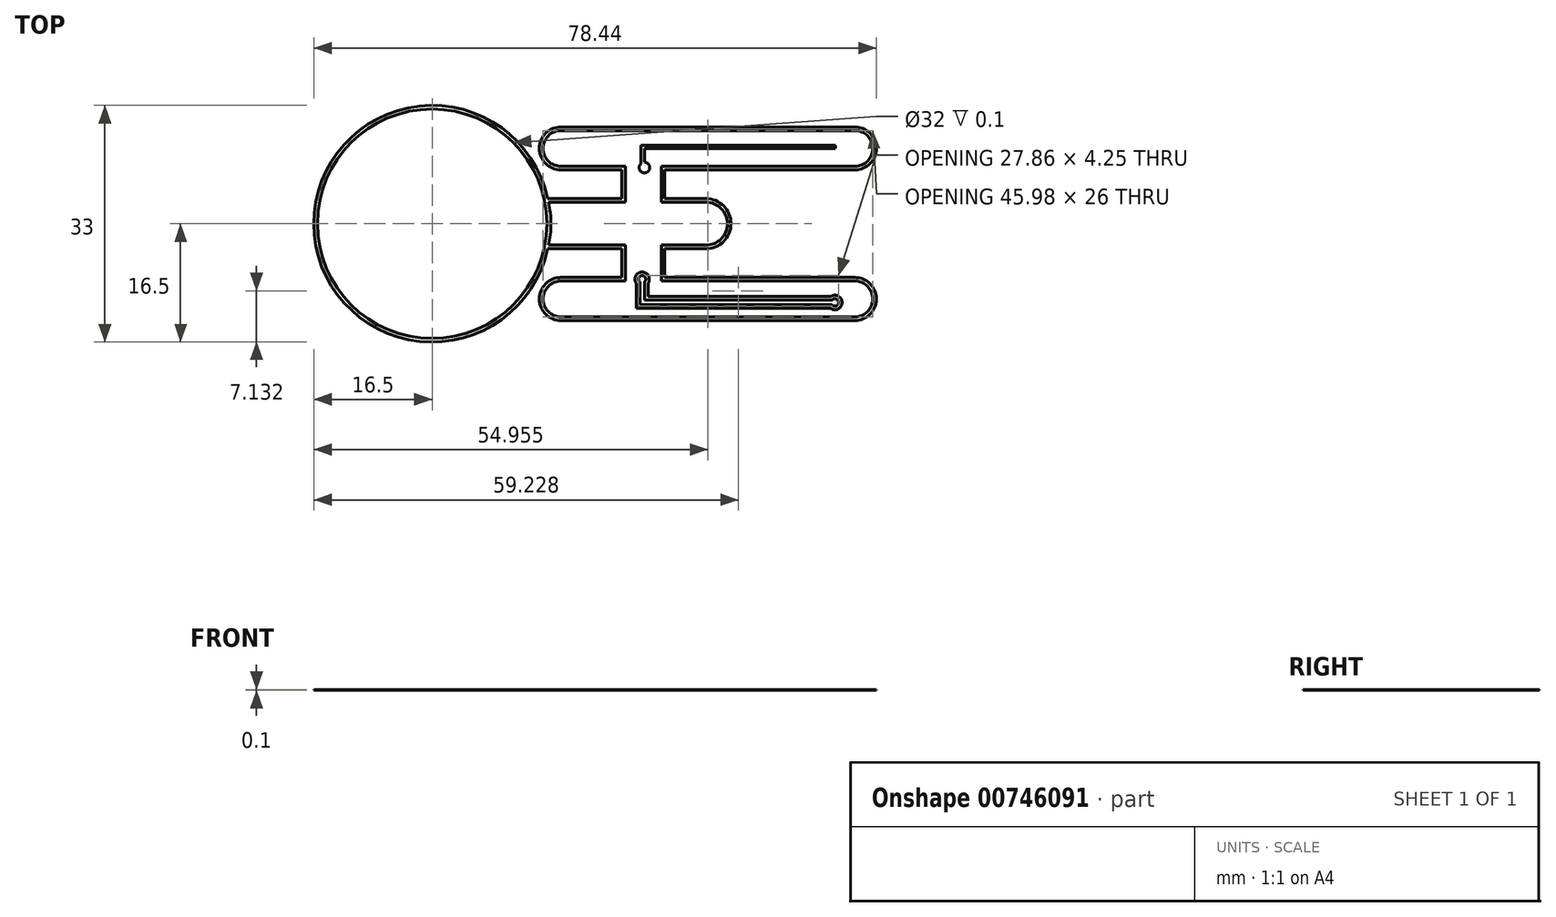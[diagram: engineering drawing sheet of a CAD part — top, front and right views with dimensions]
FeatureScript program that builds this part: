
annotation { "Feature Type Name" : "Feature", "Feature Type Description" : "" }
export const myFeature = defineFeature(function(context is Context, id is Id, definition is map)
    precondition{}
    {
        {
            var Q0;
            Q0=qCreatedBy(makeId("Top.planeOp"),FACE);
            var sketch = newSketch(context, id + "F0", { "sketchPlane" : qUnion([Q0])});
            skCircle(sketch, "E0", {"center": v(0, 0) * mm, "radius": 16 * mm});
            skLineSegment(sketch, "E1", {"start": v(16.22, 3) * mm, "end": v(26.94, 3) * mm});
            skLineSegment(sketch, "E2", {"start": v(38.16, -3) * mm, "end": v(31.94, -3) * mm});
            skLineSegment(sketch, "E3", {"start": v(31.94, 3) * mm, "end": v(31.94, 8) * mm});
            skLineSegment(sketch, "E4", {"start": v(31.94, -3) * mm, "end": v(31.94, -8) * mm});
            skLineSegment(sketch, "E5", {"start": v(26.94, 3) * mm, "end": v(26.94, 8) * mm});
            skPoint(sketch, "E5.startSnap0", {"position": v(26.94, -3) * mm});
            skLineSegment(sketch, "E6", {"start": v(26.94, -3) * mm, "end": v(26.94, -8) * mm});
            skLineSegment(sketch, "E7", {"start": v(17.97, 8) * mm, "end": v(26.94, 8) * mm});
            skLineSegment(sketch, "E8", {"start": v(58.94, 8) * mm, "end": v(58.94, 8) * mm});
            skLineSegment(sketch, "E9", {"start": v(58.94, 13) * mm, "end": v(17.97, 13) * mm});
            skLineSegment(sketch, "E10", {"start": v(17.97, -8) * mm, "end": v(26.94, -8) * mm});
            skLineSegment(sketch, "E11", {"start": v(58.94, -13) * mm, "end": v(17.97, -13) * mm});
            skArc(sketch, "E12", {"start": v(58.94, 8) * mm, "mid": v(61.44, 10.5) * mm, "end": v(58.94, 13) * mm});
            skArc(sketch, "E13", {"start": v(58.94, -13) * mm, "mid": v(61.44, -10.5) * mm, "end": v(58.94, -8) * mm});
            skArc(sketch, "E14", {"start": v(38.16, -3) * mm, "mid": v(41.16, 0) * mm, "end": v(38.16, 3) * mm});
            skLineSegment(sketch, "E15.trimOffspring", {"start": v(58.94, 13) * mm, "end": v(58.94, 13) * mm});
            skArc(sketch, "E16", {"start": v(17.97, 13) * mm, "mid": v(15.47, 10.5) * mm, "end": v(17.97, 8) * mm});
            skArc(sketch, "E17", {"start": v(17.97, -8) * mm, "mid": v(15.47, -10.5) * mm, "end": v(17.97, -13) * mm});
            skArc(sketch, "E18.0", {"start": v(58.94, 7.5) * mm, "mid": v(61.94, 10.5) * mm, "end": v(58.94, 13.5) * mm});
            skLineSegment(sketch, "E19.trimOffspring", {"start": v(31.94, 8) * mm, "end": v(58.94, 8) * mm});
            skLineSegment(sketch, "E20.trimOffspring", {"start": v(31.94, -8) * mm, "end": v(58.94, -8) * mm});
            skLineSegment(sketch, "E21.trimOffspring", {"start": v(31.94, 3) * mm, "end": v(38.16, 3) * mm});
            skLineSegment(sketch, "E22.trimOffspring", {"start": v(26.94, -3) * mm, "end": v(16.22, -3) * mm});
            skLineSegment(sketch, "E23.0", {"start": v(32.44, 7.5) * mm, "end": v(58.94, 7.5) * mm});
            skLineSegment(sketch, "E24.0", {"start": v(58.94, 13.5) * mm, "end": v(17.97, 13.5) * mm});
            skArc(sketch, "E25.0", {"start": v(17.97, 13.5) * mm, "mid": v(14.97, 10.5) * mm, "end": v(17.97, 7.5) * mm});
            skLineSegment(sketch, "E26.0", {"start": v(17.97, 7.5) * mm, "end": v(26.44, 7.5) * mm});
            skLineSegment(sketch, "E27.0", {"start": v(26.44, 3.5) * mm, "end": v(26.44, 7.5) * mm});
            skLineSegment(sketch, "E28.0", {"start": v(16.12, 3.5) * mm, "end": v(26.44, 3.5) * mm});
            skArc(sketch, "E29.0", {"start": v(16.22, 3) * mm, "mid": v(-16.5, 0) * mm, "end": v(16.22, -3) * mm});
            skLineSegment(sketch, "E30.0", {"start": v(26.44, -3.5) * mm, "end": v(16.12, -3.5) * mm});
            skLineSegment(sketch, "E31.0", {"start": v(26.44, -3.5) * mm, "end": v(26.44, -7.5) * mm});
            skLineSegment(sketch, "E32.0", {"start": v(17.97, -7.5) * mm, "end": v(26.44, -7.5) * mm});
            skArc(sketch, "E33.0", {"start": v(17.97, -7.5) * mm, "mid": v(14.97, -10.5) * mm, "end": v(17.97, -13.5) * mm});
            skLineSegment(sketch, "E34.0", {"start": v(58.94, -13.5) * mm, "end": v(17.97, -13.5) * mm});
            skArc(sketch, "E35.0", {"start": v(58.94, -13.5) * mm, "mid": v(61.94, -10.5) * mm, "end": v(58.94, -7.5) * mm});
            skLineSegment(sketch, "E36.0", {"start": v(32.44, -7.5) * mm, "end": v(58.94, -7.5) * mm});
            skLineSegment(sketch, "E37.0", {"start": v(32.44, -3.5) * mm, "end": v(32.44, -7.5) * mm});
            skLineSegment(sketch, "E38.0", {"start": v(38.16, -3.5) * mm, "end": v(32.44, -3.5) * mm});
            skArc(sketch, "E39.0", {"start": v(38.16, -3.5) * mm, "mid": v(41.66, 0) * mm, "end": v(38.16, 3.5) * mm});
            skLineSegment(sketch, "E40.0", {"start": v(32.44, 3.5) * mm, "end": v(38.16, 3.5) * mm});
            skLineSegment(sketch, "E41.0", {"start": v(32.44, 3.5) * mm, "end": v(32.44, 7.5) * mm});
            skPoint(sketch, "E42.orphan", {"position": v(15.72, -3) * mm});
            skArc(sketch, "E43", {"start": v(16.22, -3) * mm, "mid": v(16.56, 0) * mm, "end": v(16.22, 3) * mm});
            skSolve(sketch);
        }
        {
            var Q0;
            Q0=makeQuery(id+"F0.imprint","IMPRINT",FACE,{"disambiguationData":[TD([[makeQuery(id+"F0.imprint","IMPRINT",EDGE,{"derivedFrom":sQuery(id+"F0.wireOp",EDGE,"E0")}),-1.0]])]});
            var Q1;
            {var subQ1=sQuery(id+"F0.wireOp",EDGE,"E1");Q1=makeQuery(id+"F0.imprint","IMPRINT",FACE,{"disambiguationData":[TD([[makeQuery(id+"F0.imprint","IMPRINT",EDGE,{"derivedFrom":subQ1}),1.0]])]});}
            extrude(context, id + "F1", {"entities" : qUnion([Q0, Q1]), "depth" : .1 * mm, "offsetDistance" : 25 * mm});
        }
        {
            var Q0;
            Q0=qCreatedBy(makeId("Top.planeOp"),FACE);
            var sketch = newSketch(context, id + "F2", { "sketchPlane" : qUnion([Q0])});
            skLineSegment(sketch, "E44", {"start": v(56.23, 10.46) * mm, "end": v(29.6, 10.46) * mm});
            skLineSegment(sketch, "E45", {"start": v(29.6, 10.46) * mm, "end": v(29.6, 7.83) * mm});
            skLineSegment(sketch, "E46", {"start": v(55.74, -10.67) * mm, "end": v(29.6, -10.67) * mm});
            skLineSegment(sketch, "E47", {"start": v(29.6, -10.67) * mm, "end": v(29.6, -8.13) * mm});
            skLineSegment(sketch, "E48.0", {"start": v(29.1, 10.96) * mm, "end": v(29.1, 7.83) * mm});
            skLineSegment(sketch, "E48.1", {"start": v(56.23, 10.96) * mm, "end": v(29.1, 10.96) * mm});
            skLineSegment(sketch, "E49.0", {"start": v(28.96, -11.32) * mm, "end": v(28.96, -8.13) * mm});
            skLineSegment(sketch, "E49.1", {"start": v(55.74, -11.32) * mm, "end": v(28.96, -11.32) * mm});
            skLineSegment(sketch, "E50", {"start": v(29.6, 7.83) * mm, "end": v(29.1, 7.83) * mm});
            skLineSegment(sketch, "E51", {"start": v(56.23, 10.96) * mm, "end": v(56.23, 10.46) * mm});
            skCircle(sketch, "E52", {"center": v(29.6, 7.83) * mm, "radius": 0.74 * mm});
            skLineSegment(sketch, "E53.trimOffspring", {"start": v(29.04, -7.74) * mm, "end": v(28.96, -7.74) * mm});
            skArc(sketch, "E54", {"start": v(29.6, -8.13) * mm, "mid": v(29.28, -7.24) * mm, "end": v(28.96, -8.13) * mm});
            skArc(sketch, "E55", {"start": v(55.74, -11.32) * mm, "mid": v(56.66, -11) * mm, "end": v(55.74, -10.67) * mm});
            skArc(sketch, "E56.0", {"start": v(55.54, -11.82) * mm, "mid": v(57.16, -11) * mm, "end": v(55.54, -10.17) * mm});
            skLineSegment(sketch, "E56.1", {"start": v(30.1, -10.17) * mm, "end": v(30.1, -8.31) * mm});
            skArc(sketch, "E56.2", {"start": v(30.1, -8.31) * mm, "mid": v(29.28, -6.74) * mm, "end": v(28.46, -8.31) * mm});
            skLineSegment(sketch, "E56.3", {"start": v(55.54, -10.17) * mm, "end": v(30.1, -10.17) * mm});
            skLineSegment(sketch, "E56.4", {"start": v(28.46, -11.82) * mm, "end": v(28.46, -8.31) * mm});
            skLineSegment(sketch, "E56.5", {"start": v(55.54, -11.82) * mm, "end": v(28.46, -11.82) * mm});
            skSolve(sketch);
        }
        {
            var Q0;
            {var subQ2=sQuery(id+"F2.wireOp",EDGE,"E44");Q0=makeQuery(id+"F2.imprint","IMPRINT",FACE,{"disambiguationData":[TD([[makeQuery(id+"F2.imprint","IMPRINT",EDGE,{"derivedFrom":subQ2}),-1.0]])]});}
            var Q1;
            {var subQ0=sQuery(id+"F2.wireOp",EDGE,"E50");Q1=makeQuery(id+"F2.imprint","IMPRINT",FACE,{"disambiguationData":[TD([[makeQuery(id+"F2.imprint","IMPRINT",EDGE,{"derivedFrom":subQ0}),1.0]])]});}
            var Q2;
            {var subQ0=sQuery(id+"F2.wireOp",EDGE,"E50");Q2=makeQuery(id+"F2.imprint","IMPRINT",FACE,{"disambiguationData":[TD([[makeQuery(id+"F2.imprint","IMPRINT",EDGE,{"derivedFrom":subQ0}),-1.0]])]});}
            var Q3;
            Q3=makeQuery(id+"F2.imprint","IMPRINT",FACE,{"disambiguationData":[TD([[makeQuery(id+"F2.imprint","IMPRINT",EDGE,{"derivedFrom":sQuery(id+"F2.wireOp",EDGE,"E46")}),-1.0]])]});
            extrude(context, id + "F3", {"entities" : qUnion([Q0, Q1, Q2, Q3]), "depth" : .1 * mm, "offsetDistance" : 25 * mm});
        }
    });
